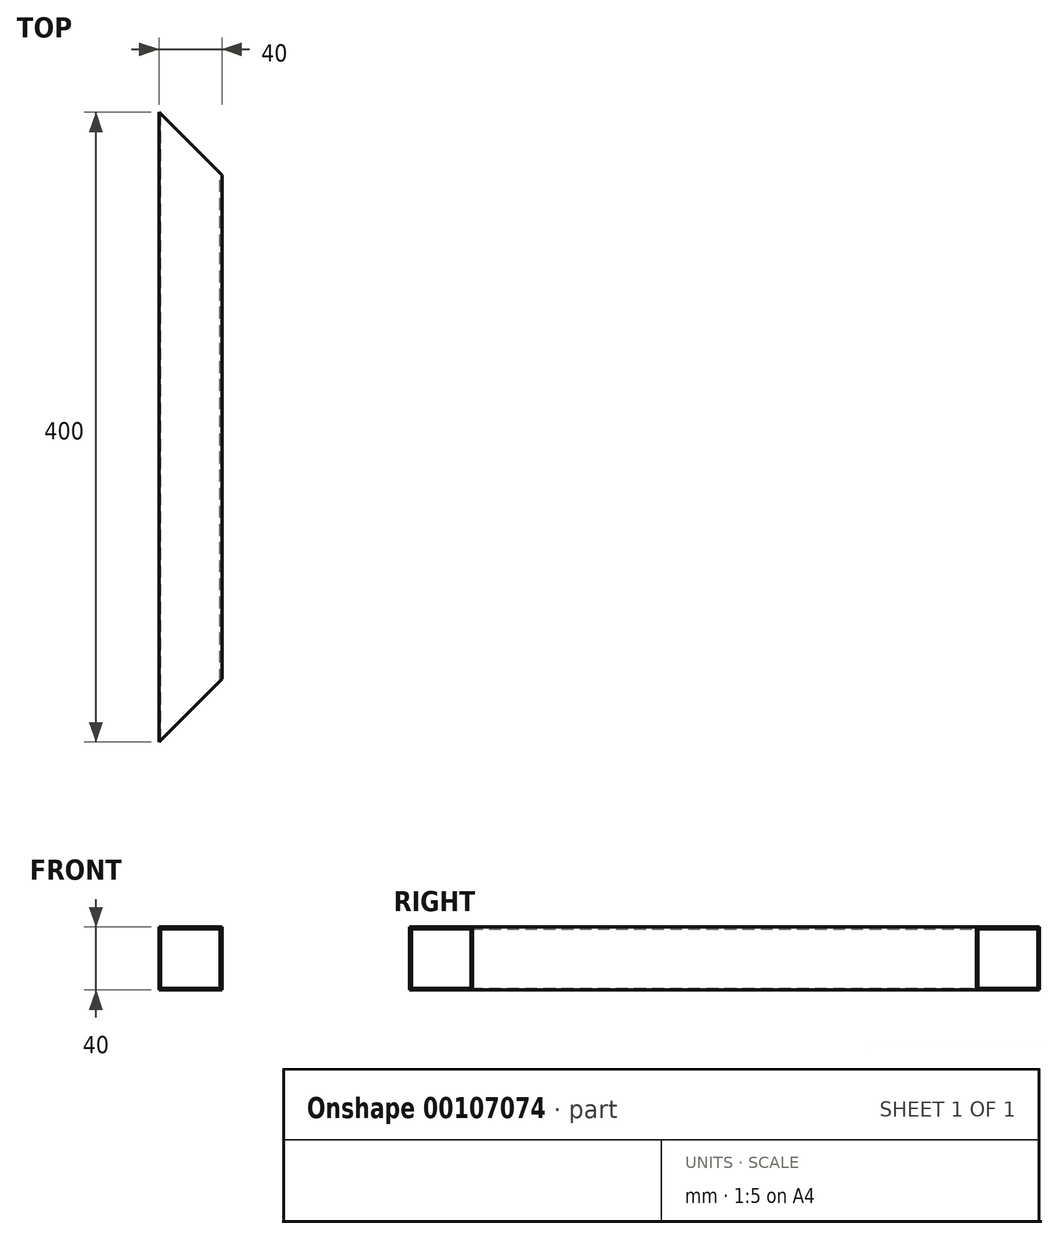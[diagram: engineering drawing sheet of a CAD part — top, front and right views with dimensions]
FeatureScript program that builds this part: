
annotation { "Feature Type Name" : "Feature", "Feature Type Description" : "" }
export const myFeature = defineFeature(function(context is Context, id is Id, definition is map)
    precondition{}
    {
        {
            var Q0;
            Q0=qCreatedBy(makeId("Front.planeOp"),FACE);
            var sketch = newSketch(context, id + "F0", { "sketchPlane" : qUnion([Q0])});
            skLineSegment(sketch, "E0.bottom", {"start": v(20, -20) * mm, "end": v(-20, -20) * mm});
            skLineSegment(sketch, "E0.top", {"start": v(20, 20) * mm, "end": v(-20, 20) * mm});
            skLineSegment(sketch, "E0.left", {"start": v(20, -20) * mm, "end": v(20, 20) * mm});
            skLineSegment(sketch, "E0.right", {"start": v(-20, -20) * mm, "end": v(-20, 20) * mm});
            skPoint(sketch, "E0.middle", {"position": v(0, 0) * mm});
            skLineSegment(sketch, "E1.bottom", {"start": v(19, -19) * mm, "end": v(-19, -19) * mm});
            skLineSegment(sketch, "E1.top", {"start": v(19, 19) * mm, "end": v(-19, 19) * mm});
            skLineSegment(sketch, "E1.left", {"start": v(19, -19) * mm, "end": v(19, 19) * mm});
            skLineSegment(sketch, "E1.right", {"start": v(-19, -19) * mm, "end": v(-19, 19) * mm});
            skSolve(sketch);
        }
        {
            var Q0;
            Q0=qSketchRegion(id+"F0",true);
            extrude(context, id + "F1", {"entities" : qUnion([Q0]), "depth" : 400 * mm});
        }
        {
            var Q0;
            Q0=makeQuery(id+"F1.opExtrude","SWEPT_FACE",FACE,{"disambiguationData":[OSD([sQuery(id+"F0.wireOp",EDGE,"E0.bottom")])]});
            var sketch = newSketch(context, id + "F2", { "sketchPlane" : qUnion([Q0])});
            skLineSegment(sketch, "E2", {"start": v(20, 40) * mm, "end": v(-20, 0) * mm});
            skLineSegment(sketch, "E3", {"start": v(-20, 0) * mm, "end": v(20, 0) * mm});
            skLineSegment(sketch, "E4", {"start": v(20, 0) * mm, "end": v(20, 40) * mm});
            skLineSegment(sketch, "E5", {"start": v(20, 400) * mm, "end": v(-20, 400) * mm});
            skLineSegment(sketch, "E6", {"start": v(-20, 400) * mm, "end": v(20, 360) * mm});
            skLineSegment(sketch, "E7", {"start": v(20, 360) * mm, "end": v(20, 400) * mm});
            skSolve(sketch);
        }
        {
            var Q0;
            Q0=qSketchRegion(id+"F2",true);
            extrude(context, id + "F3", {"entities" : qUnion([Q0]), "operationType" : NewBodyOperationType.REMOVE, "oppositeDirection" : true, "depth" : 40 * mm});
        }
    });
